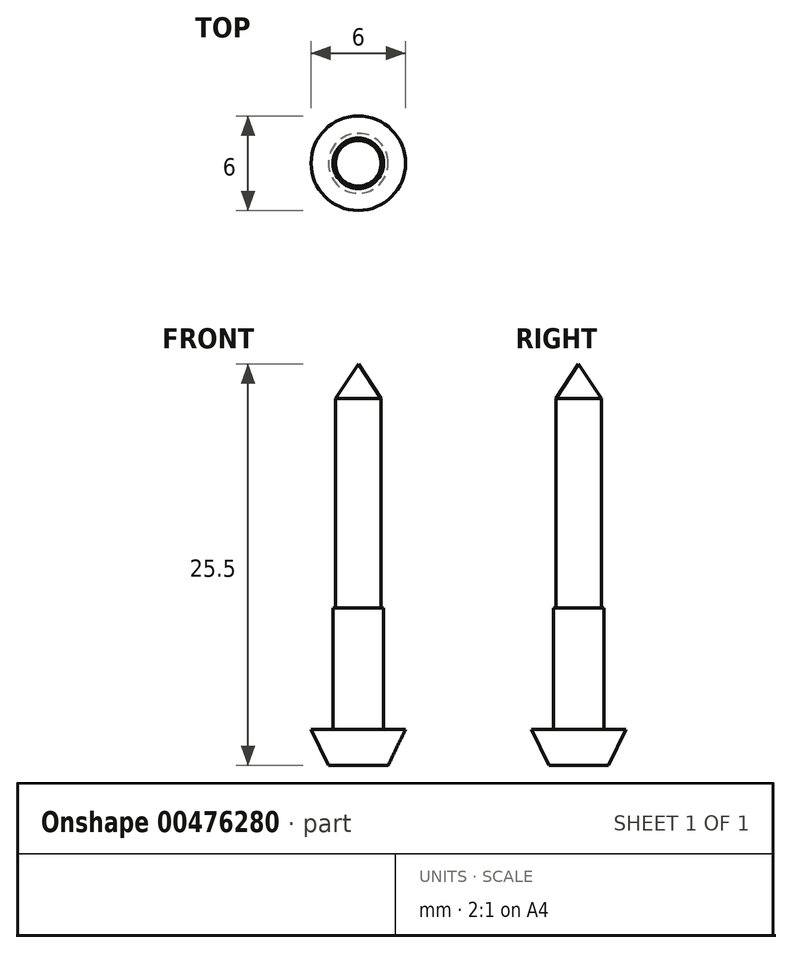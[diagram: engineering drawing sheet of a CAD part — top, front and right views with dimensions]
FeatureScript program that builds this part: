
annotation { "Feature Type Name" : "Feature", "Feature Type Description" : "" }
export const myFeature = defineFeature(function(context is Context, id is Id, definition is map)
    precondition{}
    {
        {
            var Q0;
            Q0=qCreatedBy(makeId("Front.planeOp"),FACE);
            var sketch = newSketch(context, id + "F0", { "sketchPlane" : qUnion([Q0])});
            skLineSegment(sketch, "E0", {"start": v(0, 0) * mm, "end": v(1.9, 0) * mm});
            skLineSegment(sketch, "E1", {"start": v(1.9, 0) * mm, "end": v(3, 2.3) * mm});
            skLineSegment(sketch, "E2", {"start": v(3, 2.3) * mm, "end": v(1.6, 2.3) * mm});
            skLineSegment(sketch, "E3", {"start": v(1.6, 2.3) * mm, "end": v(1.6, 10) * mm});
            skLineSegment(sketch, "E4", {"start": v(1.6, 10) * mm, "end": v(1.45, 10) * mm});
            skLineSegment(sketch, "E5", {"start": v(1.45, 10) * mm, "end": v(1.45, 23.3) * mm});
            skLineSegment(sketch, "E6", {"start": v(1.45, 23.3) * mm, "end": v(0, 25.5) * mm});
            skLineSegment(sketch, "E7", {"start": v(0, 0) * mm, "end": v(0, 25.5) * mm});
            skSolve(sketch);
        }
        {
            var Q0;
            Q0=qCreatedBy(makeId("Front.planeOp"),FACE);
            var sketch = newSketch(context, id + "F1", { "sketchPlane" : qUnion([Q0])});
            skLineSegment(sketch, "E8", {"start": v(0, 48.62) * mm, "end": v(0, -14.84) * mm});
            skSolve(sketch);
        }
        {
            var Q0;
            Q0 = qSketchRegion(id + "F0", true);
            var Q1;
            Q1=sQuery(id+"F1.wireOp",EDGE,"E8");
            revolve(context, id + "F2", {"entities" : qUnion([Q0]), "axis" : qUnion([Q1]), "revolveType" : RevolveType.FULL});
        }
    });
